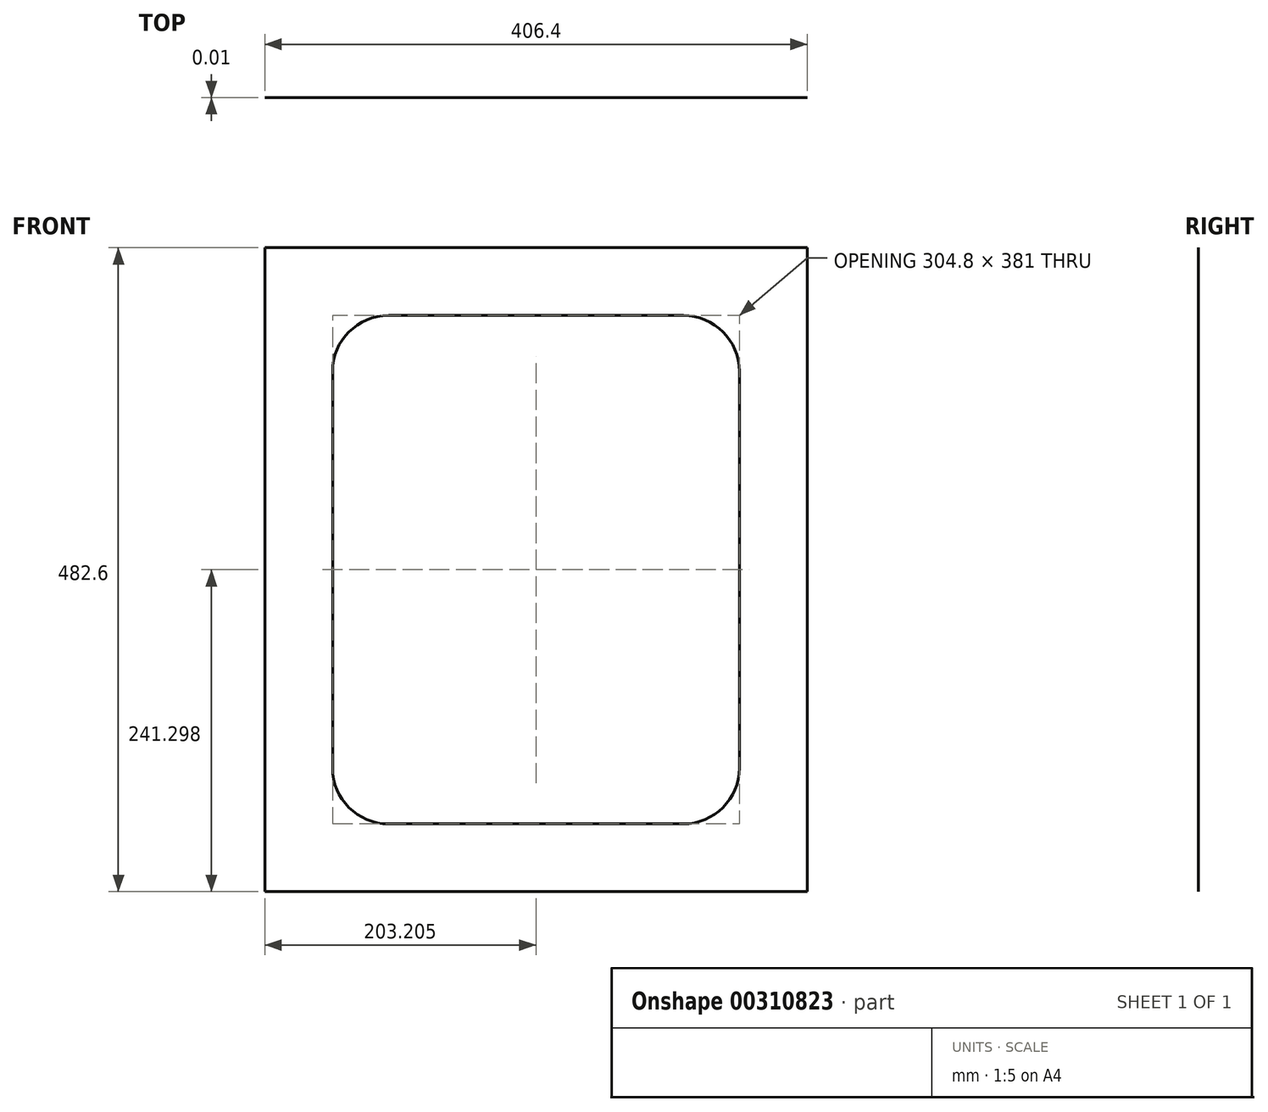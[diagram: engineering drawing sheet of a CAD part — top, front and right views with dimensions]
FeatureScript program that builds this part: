
annotation { "Feature Type Name" : "Feature", "Feature Type Description" : "" }
export const myFeature = defineFeature(function(context is Context, id is Id, definition is map)
    precondition{}
    {
        {
            var Q0;
            Q0=qCreatedBy(makeId("Front.planeOp"),FACE);
            var sketch = newSketch(context, id + "F0", { "sketchPlane" : qUnion([Q0])});
            skLineSegment(sketch, "E0.bottom", {"start": v(-338.5, 515.15) * mm, "end": v(67.9, 515.15) * mm});
            skLineSegment(sketch, "E0.top", {"start": v(-338.5, 32.55) * mm, "end": v(67.9, 32.55) * mm});
            skLineSegment(sketch, "E0.left", {"start": v(-338.5, 515.15) * mm, "end": v(-338.5, 32.55) * mm});
            skLineSegment(sketch, "E0.right", {"start": v(67.9, 515.15) * mm, "end": v(67.9, 32.55) * mm});
            skLineSegment(sketch, "E1.bottom", {"start": v(-24.8, 83.35) * mm, "end": v(-245.79, 83.35) * mm});
            skLineSegment(sketch, "E1.top", {"start": v(-24.8, 464.35) * mm, "end": v(-245.79, 464.35) * mm});
            skLineSegment(sketch, "E1.left", {"start": v(17.1, 125.26) * mm, "end": v(17.1, 422.44) * mm});
            skLineSegment(sketch, "E1.right", {"start": v(-287.7, 125.26) * mm, "end": v(-287.7, 422.44) * mm});
            skPoint(sketch, "E1.middle", {"position": v(-135.3, 273.85) * mm});
            skPoint(sketch, "E1.middle.positionSnap0", {"position": v(-135.3, 32.55) * mm});
            skPoint(sketch, "E1.middle.positionSnap1", {"position": v(67.9, 273.85) * mm});
            skPoint(sketch, "E1.centerSnap0", {"position": v(-135.3, 32.55) * mm});
            skPoint(sketch, "E1.centerSnap1", {"position": v(67.9, 273.85) * mm});
            skPoint(sketch, "E2.visualSharp", {"position": v(-287.7, 464.35) * mm});
            skArc(sketch, "E2.filletArc", {"start": v(-245.79, 464.35) * mm, "mid": v(-275.42, 452.07) * mm, "end": v(-287.7, 422.44) * mm});
            skPoint(sketch, "E3.visualSharp", {"position": v(-287.7, 83.35) * mm});
            skArc(sketch, "E3.filletArc", {"start": v(-287.7, 125.26) * mm, "mid": v(-275.42, 95.62) * mm, "end": v(-245.79, 83.35) * mm});
            skPoint(sketch, "E4.visualSharp", {"position": v(17.1, 83.35) * mm});
            skArc(sketch, "E4.filletArc", {"start": v(-24.8, 83.35) * mm, "mid": v(4.83, 95.62) * mm, "end": v(17.1, 125.26) * mm});
            skPoint(sketch, "E5.visualSharp", {"position": v(17.1, 464.35) * mm});
            skArc(sketch, "E5.filletArc", {"start": v(17.1, 422.44) * mm, "mid": v(4.83, 452.07) * mm, "end": v(-24.8, 464.35) * mm});
            skSolve(sketch);
        }
        {
            var Q0;
            Q0=makeQuery(id+"F0.imprint","IMPRINT",FACE,{"disambiguationData":[TD([[makeQuery(id+"F0.imprint","IMPRINT",EDGE,{"derivedFrom":sQuery(id+"F0.wireOp",EDGE,"E0.bottom")}),-1.0]])]});
            extrude(context, id + "F1", {"entities" : qUnion([Q0]), "depth" : 3 / 203.2 * mm});
        }
    });
